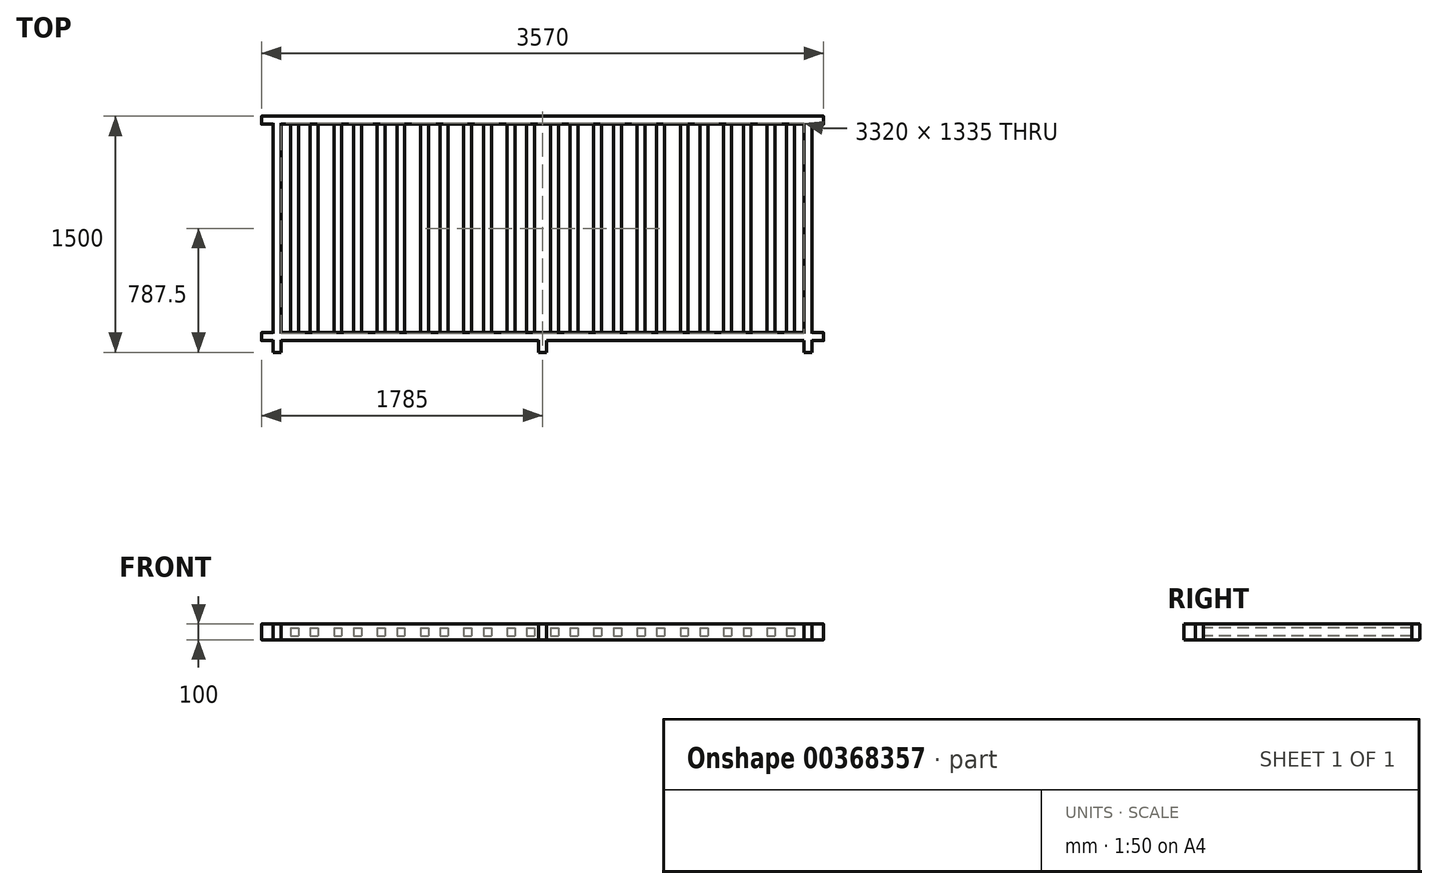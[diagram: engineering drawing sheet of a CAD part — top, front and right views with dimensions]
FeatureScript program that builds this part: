
annotation { "Feature Type Name" : "Feature", "Feature Type Description" : "" }
export const myFeature = defineFeature(function(context is Context, id is Id, definition is map)
    precondition{}
    {
        {
            var Q0;
            Q0=qCreatedBy(makeId("Top.planeOp"),FACE);
            var sketch = newSketch(context, id + "F0", { "sketchPlane" : qUnion([Q0])});
            skLineSegment(sketch, "E0.bottom", {"start": v(0, 0) * mm, "end": v(3570, 0) * mm, "construction": true});
            skLineSegment(sketch, "E0.top", {"start": v(0, 1500) * mm, "end": v(3570, 1500) * mm, "construction": true});
            skLineSegment(sketch, "E0.left", {"start": v(0, 0) * mm, "end": v(0, 1500) * mm, "construction": true});
            skLineSegment(sketch, "E0.right", {"start": v(3570, 0) * mm, "end": v(3570, 1500) * mm, "construction": true});
            skLineSegment(sketch, "E1.bottom", {"start": v(0, 1500) * mm, "end": v(3570, 1500) * mm});
            skLineSegment(sketch, "E1.top", {"start": v(0, 1450) * mm, "end": v(3570, 1450) * mm});
            skLineSegment(sketch, "E1.left", {"start": v(0, 1500) * mm, "end": v(0, 1450) * mm});
            skLineSegment(sketch, "E1.right", {"start": v(3570, 1500) * mm, "end": v(3570, 1450) * mm});
            skLineSegment(sketch, "E2.bottom", {"start": v(0, 125) * mm, "end": v(3570, 125) * mm});
            skLineSegment(sketch, "E2.top", {"start": v(0, 75) * mm, "end": v(3570, 75) * mm});
            skLineSegment(sketch, "E2.left", {"start": v(0, 125) * mm, "end": v(0, 75) * mm});
            skLineSegment(sketch, "E2.right", {"start": v(3570, 125) * mm, "end": v(3570, 75) * mm});
            skLineSegment(sketch, "E3.bottom", {"start": v(75, 1500) * mm, "end": v(125, 1500) * mm});
            skLineSegment(sketch, "E3.top", {"start": v(75, 0) * mm, "end": v(125, 0) * mm});
            skLineSegment(sketch, "E3.left", {"start": v(75, 1500) * mm, "end": v(75, 0) * mm});
            skLineSegment(sketch, "E3.right", {"start": v(125, 1500) * mm, "end": v(125, 0) * mm});
            skLineSegment(sketch, "E4.bottom", {"start": v(3445, 1500) * mm, "end": v(3495, 1500) * mm});
            skLineSegment(sketch, "E4.top", {"start": v(3445, 0) * mm, "end": v(3495, 0) * mm});
            skLineSegment(sketch, "E4.left", {"start": v(3445, 1500) * mm, "end": v(3445, 0) * mm});
            skLineSegment(sketch, "E4.right", {"start": v(3495, 1500) * mm, "end": v(3495, 0) * mm});
            skLineSegment(sketch, "E5.bottom", {"start": v(1810, 0) * mm, "end": v(1760, 0) * mm});
            skLineSegment(sketch, "E5.left", {"start": v(1810, 0) * mm, "end": v(1810, 75) * mm});
            skLineSegment(sketch, "E5.right", {"start": v(1760, 0) * mm, "end": v(1760, 75) * mm});
            skLineSegment(sketch, "E6", {"start": v(3495, 1450) * mm, "end": v(3495, 125) * mm, "construction": true});
            skLineSegment(sketch, "E7", {"start": v(75, 1450) * mm, "end": v(75, 125) * mm, "construction": true});
            skSolve(sketch);
        }
        {
            var Q0;
            Q0=qSketchRegion(id+"F0",true);
            extrude(context, id + "F1", {"entities" : qUnion([Q0]), "depth" : 75 * mm, "hasSecondDirection" : true, "secondDirectionOppositeDirection" : true, "secondDirectionDepth" : 25 * mm});
        }
        {
            var Q0;
            {var subQ0=sQuery(id+"F0.wireOp",EDGE,"E1.top");Q0=makeQuery(id+"F1.opExtrude","CAP_EDGE",EDGE,{"disambiguationData":[OSD([subQ0]),TDD([makeQuery(id+"F0.imprint","IMPRINT",EDGE,{"disambiguationData":[TD([[makeQuery(id+"F0.imprint","INTERSECT",VERTEX,{"derivedFrom":[subQ0,sQuery(id+"F0.wireOp",EDGE,"E3.right")]}),-1.0]])],"derivedFrom":subQ0})])],"isStart":false});}
            var Q1;
            Q1=makeQuery(id+"F1.opExtrude","CAP_EDGE",EDGE,{"disambiguationData":[OSD([sQuery(id+"F0.wireOp",EDGE,"E1.bottom"),sQuery(id+"F0.wireOp",EDGE,"E3.bottom"),sQuery(id+"F0.wireOp",EDGE,"E4.bottom")])],"isStart":false});
            var Q2;
            {var subQ0=sQuery(id+"F0.wireOp",EDGE,"E2.bottom");Q2=makeQuery(id+"F1.opExtrude","CAP_EDGE",EDGE,{"disambiguationData":[OSD([subQ0]),TDD([makeQuery(id+"F0.imprint","IMPRINT",EDGE,{"disambiguationData":[TD([[makeQuery(id+"F0.imprint","INTERSECT",VERTEX,{"derivedFrom":[subQ0,sQuery(id+"F0.wireOp",EDGE,"E3.right")]}),-1.0]])],"derivedFrom":subQ0})])],"isStart":false});}
            var Q3;
            {var subQ0=sQuery(id+"F0.wireOp",EDGE,"E2.top");Q3=makeQuery(id+"F1.opExtrude","CAP_EDGE",EDGE,{"disambiguationData":[OSD([subQ0]),TDD([makeQuery(id+"F0.imprint","IMPRINT",EDGE,{"disambiguationData":[TD([[makeQuery(id+"F0.imprint","INTERSECT",VERTEX,{"derivedFrom":[subQ0,sQuery(id+"F0.wireOp",EDGE,"E3.right")]}),-1.0]])],"derivedFrom":subQ0})])],"isStart":false});}
            var Q4;
            {var subQ0=sQuery(id+"F0.wireOp",EDGE,"E2.top");Q4=makeQuery(id+"F1.opExtrude","CAP_EDGE",EDGE,{"disambiguationData":[OSD([subQ0]),TDD([makeQuery(id+"F0.imprint","IMPRINT",EDGE,{"disambiguationData":[TD([[makeQuery(id+"F0.imprint","INTERSECT",VERTEX,{"derivedFrom":[subQ0,sQuery(id+"F0.wireOp",EDGE,"E2.left")]}),-1.0]])],"derivedFrom":subQ0})])],"isStart":false});}
            var Q5;
            {var subQ0=sQuery(id+"F0.wireOp",EDGE,"E2.bottom");Q5=makeQuery(id+"F1.opExtrude","CAP_EDGE",EDGE,{"disambiguationData":[OSD([subQ0]),TDD([makeQuery(id+"F0.imprint","IMPRINT",EDGE,{"disambiguationData":[TD([[makeQuery(id+"F0.imprint","INTERSECT",VERTEX,{"derivedFrom":[subQ0,sQuery(id+"F0.wireOp",EDGE,"E2.left")]}),-1.0]])],"derivedFrom":subQ0})])],"isStart":false});}
            var Q6;
            {var subQ0=sQuery(id+"F0.wireOp",EDGE,"E2.bottom");Q6=makeQuery(id+"F1.opExtrude","CAP_EDGE",EDGE,{"disambiguationData":[OSD([subQ0]),TDD([makeQuery(id+"F0.imprint","IMPRINT",EDGE,{"disambiguationData":[TD([[makeQuery(id+"F0.imprint","INTERSECT",VERTEX,{"derivedFrom":[subQ0,sQuery(id+"F0.wireOp",EDGE,"E2.right")]}),1.0]])],"derivedFrom":subQ0})])],"isStart":false});}
            var Q7;
            {var subQ0=sQuery(id+"F0.wireOp",EDGE,"E2.top");Q7=makeQuery(id+"F1.opExtrude","CAP_EDGE",EDGE,{"disambiguationData":[OSD([subQ0]),TDD([makeQuery(id+"F0.imprint","IMPRINT",EDGE,{"disambiguationData":[TD([[makeQuery(id+"F0.imprint","INTERSECT",VERTEX,{"derivedFrom":[subQ0,sQuery(id+"F0.wireOp",EDGE,"E2.right")]}),1.0]])],"derivedFrom":subQ0})])],"isStart":false});}
            var Q8;
            {var subQ0=sQuery(id+"F0.wireOp",EDGE,"E1.top");Q8=makeQuery(id+"F1.opExtrude","CAP_EDGE",EDGE,{"disambiguationData":[OSD([subQ0]),TDD([makeQuery(id+"F0.imprint","IMPRINT",EDGE,{"disambiguationData":[TD([[makeQuery(id+"F0.imprint","INTERSECT",VERTEX,{"derivedFrom":[subQ0,sQuery(id+"F0.wireOp",EDGE,"E1.right")]}),1.0]])],"derivedFrom":subQ0})])],"isStart":false});}
            var Q9;
            {var subQ0=sQuery(id+"F0.wireOp",EDGE,"E1.top");Q9=makeQuery(id+"F1.opExtrude","CAP_EDGE",EDGE,{"disambiguationData":[OSD([subQ0]),TDD([makeQuery(id+"F0.imprint","IMPRINT",EDGE,{"disambiguationData":[TD([[makeQuery(id+"F0.imprint","INTERSECT",VERTEX,{"derivedFrom":[subQ0,sQuery(id+"F0.wireOp",EDGE,"E1.left")]}),-1.0]])],"derivedFrom":subQ0})])],"isStart":false});}
            var Q10;
            Q10=makeQuery(id+"F1.opExtrude","CAP_EDGE",EDGE,{"disambiguationData":[OSD([sQuery(id+"F0.wireOp",EDGE,"E1.bottom"),sQuery(id+"F0.wireOp",EDGE,"E3.bottom"),sQuery(id+"F0.wireOp",EDGE,"E4.bottom")])],"isStart":true});
            var Q11;
            {var subQ0=sQuery(id+"F0.wireOp",EDGE,"E1.top");Q11=makeQuery(id+"F1.opExtrude","CAP_EDGE",EDGE,{"disambiguationData":[OSD([subQ0]),TDD([makeQuery(id+"F0.imprint","IMPRINT",EDGE,{"disambiguationData":[TD([[makeQuery(id+"F0.imprint","INTERSECT",VERTEX,{"derivedFrom":[subQ0,sQuery(id+"F0.wireOp",EDGE,"E3.right")]}),-1.0]])],"derivedFrom":subQ0})])],"isStart":true});}
            var Q12;
            {var subQ0=sQuery(id+"F0.wireOp",EDGE,"E1.top");Q12=makeQuery(id+"F1.opExtrude","CAP_EDGE",EDGE,{"disambiguationData":[OSD([subQ0]),TDD([makeQuery(id+"F0.imprint","IMPRINT",EDGE,{"disambiguationData":[TD([[makeQuery(id+"F0.imprint","INTERSECT",VERTEX,{"derivedFrom":[subQ0,sQuery(id+"F0.wireOp",EDGE,"E1.right")]}),1.0]])],"derivedFrom":subQ0})])],"isStart":true});}
            var Q13;
            {var subQ0=sQuery(id+"F0.wireOp",EDGE,"E2.top");Q13=makeQuery(id+"F1.opExtrude","CAP_EDGE",EDGE,{"disambiguationData":[OSD([subQ0]),TDD([makeQuery(id+"F0.imprint","IMPRINT",EDGE,{"disambiguationData":[TD([[makeQuery(id+"F0.imprint","INTERSECT",VERTEX,{"derivedFrom":[subQ0,sQuery(id+"F0.wireOp",EDGE,"E2.right")]}),1.0]])],"derivedFrom":subQ0})])],"isStart":true});}
            var Q14;
            {var subQ0=sQuery(id+"F0.wireOp",EDGE,"E2.bottom");Q14=makeQuery(id+"F1.opExtrude","CAP_EDGE",EDGE,{"disambiguationData":[OSD([subQ0]),TDD([makeQuery(id+"F0.imprint","IMPRINT",EDGE,{"disambiguationData":[TD([[makeQuery(id+"F0.imprint","INTERSECT",VERTEX,{"derivedFrom":[subQ0,sQuery(id+"F0.wireOp",EDGE,"E2.right")]}),1.0]])],"derivedFrom":subQ0})])],"isStart":true});}
            var Q15;
            {var subQ0=sQuery(id+"F0.wireOp",EDGE,"E2.bottom");Q15=makeQuery(id+"F1.opExtrude","CAP_EDGE",EDGE,{"disambiguationData":[OSD([subQ0]),TDD([makeQuery(id+"F0.imprint","IMPRINT",EDGE,{"disambiguationData":[TD([[makeQuery(id+"F0.imprint","INTERSECT",VERTEX,{"derivedFrom":[subQ0,sQuery(id+"F0.wireOp",EDGE,"E3.right")]}),-1.0]])],"derivedFrom":subQ0})])],"isStart":true});}
            var Q16;
            {var subQ0=sQuery(id+"F0.wireOp",EDGE,"E2.top");Q16=makeQuery(id+"F1.opExtrude","CAP_EDGE",EDGE,{"disambiguationData":[OSD([subQ0]),TDD([makeQuery(id+"F0.imprint","IMPRINT",EDGE,{"disambiguationData":[TD([[makeQuery(id+"F0.imprint","INTERSECT",VERTEX,{"derivedFrom":[subQ0,sQuery(id+"F0.wireOp",EDGE,"E3.right")]}),-1.0]])],"derivedFrom":subQ0})])],"isStart":true});}
            var Q17;
            {var subQ0=sQuery(id+"F0.wireOp",EDGE,"E2.bottom");Q17=makeQuery(id+"F1.opExtrude","CAP_EDGE",EDGE,{"disambiguationData":[OSD([subQ0]),TDD([makeQuery(id+"F0.imprint","IMPRINT",EDGE,{"disambiguationData":[TD([[makeQuery(id+"F0.imprint","INTERSECT",VERTEX,{"derivedFrom":[subQ0,sQuery(id+"F0.wireOp",EDGE,"E2.left")]}),-1.0]])],"derivedFrom":subQ0})])],"isStart":true});}
            var Q18;
            {var subQ0=sQuery(id+"F0.wireOp",EDGE,"E2.top");Q18=makeQuery(id+"F1.opExtrude","CAP_EDGE",EDGE,{"disambiguationData":[OSD([subQ0]),TDD([makeQuery(id+"F0.imprint","IMPRINT",EDGE,{"disambiguationData":[TD([[makeQuery(id+"F0.imprint","INTERSECT",VERTEX,{"derivedFrom":[subQ0,sQuery(id+"F0.wireOp",EDGE,"E2.left")]}),-1.0]])],"derivedFrom":subQ0})])],"isStart":true});}
            var Q19;
            {var subQ0=sQuery(id+"F0.wireOp",EDGE,"E1.top");Q19=makeQuery(id+"F1.opExtrude","CAP_EDGE",EDGE,{"disambiguationData":[OSD([subQ0]),TDD([makeQuery(id+"F0.imprint","IMPRINT",EDGE,{"disambiguationData":[TD([[makeQuery(id+"F0.imprint","INTERSECT",VERTEX,{"derivedFrom":[subQ0,sQuery(id+"F0.wireOp",EDGE,"E1.left")]}),-1.0]])],"derivedFrom":subQ0})])],"isStart":true});}
            fillet(context, id + "F2", {"entities" : qUnion([Q0, Q1, Q2, Q3, Q4, Q5, Q6, Q7, Q8, Q9, Q10, Q11, Q12, Q13, Q14, Q15, Q16, Q17, Q18, Q19]), "radius" : 5 * mm, "tangentPropagation" : true, "allowEdgeOverflow" : false});
        }
        {
            var Q0;
            Q0=qCreatedBy(makeId("Top.planeOp"),FACE);
            var sketch = newSketch(context, id + "F3", { "sketchPlane" : qUnion([Q0])});
            skLineSegment(sketch, "E8.bottom", {"start": v(185, 1450) * mm, "end": v(235, 1450) * mm});
            skLineSegment(sketch, "E8.top", {"start": v(185, 125) * mm, "end": v(235, 125) * mm});
            skLineSegment(sketch, "E8.left", {"start": v(185, 1450) * mm, "end": v(185, 125) * mm});
            skLineSegment(sketch, "E8.right", {"start": v(235, 1450) * mm, "end": v(235, 125) * mm});
            skLineSegment(sketch, "E9.bottom", {"start": v(310, 1450) * mm, "end": v(360, 1450) * mm});
            skLineSegment(sketch, "E9.top", {"start": v(310, 125) * mm, "end": v(360, 125) * mm});
            skLineSegment(sketch, "E9.left", {"start": v(310, 1450) * mm, "end": v(310, 125) * mm});
            skLineSegment(sketch, "E9.right", {"start": v(360, 1450) * mm, "end": v(360, 125) * mm});
            skLineSegment(sketch, "E10", {"start": v(235, 125) * mm, "end": v(387, 125) * mm, "construction": true});
            skLineSegment(sketch, "E11", {"start": v(235, 1450) * mm, "end": v(386.34, 1450) * mm, "construction": true});
            skLineSegment(sketch, "E12.1.0.0", {"start": v(635, 1450) * mm, "end": v(635, 125) * mm});
            skLineSegment(sketch, "E12.1.0.1", {"start": v(585, 1450) * mm, "end": v(585, 125) * mm});
            skLineSegment(sketch, "E12.1.0.2", {"start": v(510, 1450) * mm, "end": v(510, 125) * mm});
            skLineSegment(sketch, "E12.1.0.3", {"start": v(460, 1450) * mm, "end": v(460, 125) * mm});
            skLineSegment(sketch, "E12.1.0.4", {"start": v(460, 125) * mm, "end": v(510, 125) * mm});
            skLineSegment(sketch, "E12.1.0.5", {"start": v(460, 1450) * mm, "end": v(510, 1450) * mm});
            skLineSegment(sketch, "E12.1.0.6", {"start": v(585, 125) * mm, "end": v(635, 125) * mm});
            skLineSegment(sketch, "E12.1.0.7", {"start": v(585, 1450) * mm, "end": v(635, 1450) * mm});
            skLineSegment(sketch, "E12.2.0.0", {"start": v(910, 1450) * mm, "end": v(910, 125) * mm});
            skLineSegment(sketch, "E12.2.0.1", {"start": v(860, 1450) * mm, "end": v(860, 125) * mm});
            skLineSegment(sketch, "E12.2.0.2", {"start": v(785, 1450) * mm, "end": v(785, 125) * mm});
            skLineSegment(sketch, "E12.2.0.3", {"start": v(735, 1450) * mm, "end": v(735, 125) * mm});
            skLineSegment(sketch, "E12.2.0.4", {"start": v(735, 125) * mm, "end": v(785, 125) * mm});
            skLineSegment(sketch, "E12.2.0.5", {"start": v(735, 1450) * mm, "end": v(785, 1450) * mm});
            skLineSegment(sketch, "E12.2.0.6", {"start": v(860, 125) * mm, "end": v(910, 125) * mm});
            skLineSegment(sketch, "E12.2.0.7", {"start": v(860, 1450) * mm, "end": v(910, 1450) * mm});
            skLineSegment(sketch, "E12.3.0.0", {"start": v(1185, 1450) * mm, "end": v(1185, 125) * mm});
            skLineSegment(sketch, "E12.3.0.1", {"start": v(1135, 1450) * mm, "end": v(1135, 125) * mm});
            skLineSegment(sketch, "E12.3.0.2", {"start": v(1060, 1450) * mm, "end": v(1060, 125) * mm});
            skLineSegment(sketch, "E12.3.0.3", {"start": v(1010, 1450) * mm, "end": v(1010, 125) * mm});
            skLineSegment(sketch, "E12.3.0.4", {"start": v(1010, 125) * mm, "end": v(1060, 125) * mm});
            skLineSegment(sketch, "E12.3.0.5", {"start": v(1010, 1450) * mm, "end": v(1060, 1450) * mm});
            skLineSegment(sketch, "E12.3.0.6", {"start": v(1135, 125) * mm, "end": v(1185, 125) * mm});
            skLineSegment(sketch, "E12.3.0.7", {"start": v(1135, 1450) * mm, "end": v(1185, 1450) * mm});
            skLineSegment(sketch, "E12.4.0.0", {"start": v(1460, 1450) * mm, "end": v(1460, 125) * mm});
            skLineSegment(sketch, "E12.4.0.1", {"start": v(1410, 1450) * mm, "end": v(1410, 125) * mm});
            skLineSegment(sketch, "E12.4.0.2", {"start": v(1335, 1450) * mm, "end": v(1335, 125) * mm});
            skLineSegment(sketch, "E12.4.0.3", {"start": v(1285, 1450) * mm, "end": v(1285, 125) * mm});
            skLineSegment(sketch, "E12.4.0.4", {"start": v(1285, 125) * mm, "end": v(1335, 125) * mm});
            skLineSegment(sketch, "E12.4.0.5", {"start": v(1285, 1450) * mm, "end": v(1335, 1450) * mm});
            skLineSegment(sketch, "E12.4.0.6", {"start": v(1410, 125) * mm, "end": v(1460, 125) * mm});
            skLineSegment(sketch, "E12.4.0.7", {"start": v(1410, 1450) * mm, "end": v(1460, 1450) * mm});
            skLineSegment(sketch, "E12.5.0.0", {"start": v(1735, 1450) * mm, "end": v(1735, 125) * mm});
            skLineSegment(sketch, "E12.5.0.1", {"start": v(1685, 1450) * mm, "end": v(1685, 125) * mm});
            skLineSegment(sketch, "E12.5.0.2", {"start": v(1610, 1450) * mm, "end": v(1610, 125) * mm});
            skLineSegment(sketch, "E12.5.0.3", {"start": v(1560, 1450) * mm, "end": v(1560, 125) * mm});
            skLineSegment(sketch, "E12.5.0.4", {"start": v(1560, 125) * mm, "end": v(1610, 125) * mm});
            skLineSegment(sketch, "E12.5.0.5", {"start": v(1560, 1450) * mm, "end": v(1610, 1450) * mm});
            skLineSegment(sketch, "E12.5.0.6", {"start": v(1685, 125) * mm, "end": v(1735, 125) * mm});
            skLineSegment(sketch, "E12.5.0.7", {"start": v(1685, 1450) * mm, "end": v(1735, 1450) * mm});
            skLineSegment(sketch, "E12.6.0.0", {"start": v(2010, 1450) * mm, "end": v(2010, 125) * mm});
            skLineSegment(sketch, "E12.6.0.1", {"start": v(1960, 1450) * mm, "end": v(1960, 125) * mm});
            skLineSegment(sketch, "E12.6.0.2", {"start": v(1885, 1450) * mm, "end": v(1885, 125) * mm});
            skLineSegment(sketch, "E12.6.0.3", {"start": v(1835, 1450) * mm, "end": v(1835, 125) * mm});
            skLineSegment(sketch, "E12.6.0.4", {"start": v(1835, 125) * mm, "end": v(1885, 125) * mm});
            skLineSegment(sketch, "E12.6.0.5", {"start": v(1835, 1450) * mm, "end": v(1885, 1450) * mm});
            skLineSegment(sketch, "E12.6.0.6", {"start": v(1960, 125) * mm, "end": v(2010, 125) * mm});
            skLineSegment(sketch, "E12.6.0.7", {"start": v(1960, 1450) * mm, "end": v(2010, 1450) * mm});
            skLineSegment(sketch, "E12.7.0.0", {"start": v(2285, 1450) * mm, "end": v(2285, 125) * mm});
            skLineSegment(sketch, "E12.7.0.1", {"start": v(2235, 1450) * mm, "end": v(2235, 125) * mm});
            skLineSegment(sketch, "E12.7.0.2", {"start": v(2160, 1450) * mm, "end": v(2160, 125) * mm});
            skLineSegment(sketch, "E12.7.0.3", {"start": v(2110, 1450) * mm, "end": v(2110, 125) * mm});
            skLineSegment(sketch, "E12.7.0.4", {"start": v(2110, 125) * mm, "end": v(2160, 125) * mm});
            skLineSegment(sketch, "E12.7.0.5", {"start": v(2110, 1450) * mm, "end": v(2160, 1450) * mm});
            skLineSegment(sketch, "E12.7.0.6", {"start": v(2235, 125) * mm, "end": v(2285, 125) * mm});
            skLineSegment(sketch, "E12.7.0.7", {"start": v(2235, 1450) * mm, "end": v(2285, 1450) * mm});
            skLineSegment(sketch, "E12.8.0.0", {"start": v(2560, 1450) * mm, "end": v(2560, 125) * mm});
            skLineSegment(sketch, "E12.8.0.1", {"start": v(2510, 1450) * mm, "end": v(2510, 125) * mm});
            skLineSegment(sketch, "E12.8.0.2", {"start": v(2435, 1450) * mm, "end": v(2435, 125) * mm});
            skLineSegment(sketch, "E12.8.0.3", {"start": v(2385, 1450) * mm, "end": v(2385, 125) * mm});
            skLineSegment(sketch, "E12.8.0.4", {"start": v(2385, 125) * mm, "end": v(2435, 125) * mm});
            skLineSegment(sketch, "E12.8.0.5", {"start": v(2385, 1450) * mm, "end": v(2435, 1450) * mm});
            skLineSegment(sketch, "E12.8.0.6", {"start": v(2510, 125) * mm, "end": v(2560, 125) * mm});
            skLineSegment(sketch, "E12.8.0.7", {"start": v(2510, 1450) * mm, "end": v(2560, 1450) * mm});
            skLineSegment(sketch, "E12.9.0.0", {"start": v(2835, 1450) * mm, "end": v(2835, 125) * mm});
            skLineSegment(sketch, "E12.9.0.1", {"start": v(2785, 1450) * mm, "end": v(2785, 125) * mm});
            skLineSegment(sketch, "E12.9.0.2", {"start": v(2710, 1450) * mm, "end": v(2710, 125) * mm});
            skLineSegment(sketch, "E12.9.0.3", {"start": v(2660, 1450) * mm, "end": v(2660, 125) * mm});
            skLineSegment(sketch, "E12.9.0.4", {"start": v(2660, 125) * mm, "end": v(2710, 125) * mm});
            skLineSegment(sketch, "E12.9.0.5", {"start": v(2660, 1450) * mm, "end": v(2710, 1450) * mm});
            skLineSegment(sketch, "E12.9.0.6", {"start": v(2785, 125) * mm, "end": v(2835, 125) * mm});
            skLineSegment(sketch, "E12.9.0.7", {"start": v(2785, 1450) * mm, "end": v(2835, 1450) * mm});
            skLineSegment(sketch, "E12.10.0.0", {"start": v(3110, 1450) * mm, "end": v(3110, 125) * mm});
            skLineSegment(sketch, "E12.10.0.1", {"start": v(3060, 1450) * mm, "end": v(3060, 125) * mm});
            skLineSegment(sketch, "E12.10.0.2", {"start": v(2985, 1450) * mm, "end": v(2985, 125) * mm});
            skLineSegment(sketch, "E12.10.0.3", {"start": v(2935, 1450) * mm, "end": v(2935, 125) * mm});
            skLineSegment(sketch, "E12.10.0.4", {"start": v(2935, 125) * mm, "end": v(2985, 125) * mm});
            skLineSegment(sketch, "E12.10.0.5", {"start": v(2935, 1450) * mm, "end": v(2985, 1450) * mm});
            skLineSegment(sketch, "E12.10.0.6", {"start": v(3060, 125) * mm, "end": v(3110, 125) * mm});
            skLineSegment(sketch, "E12.10.0.7", {"start": v(3060, 1450) * mm, "end": v(3110, 1450) * mm});
            skLineSegment(sketch, "E12.11.0.0", {"start": v(3385, 1450) * mm, "end": v(3385, 125) * mm});
            skLineSegment(sketch, "E12.11.0.1", {"start": v(3335, 1450) * mm, "end": v(3335, 125) * mm});
            skLineSegment(sketch, "E12.11.0.2", {"start": v(3260, 1450) * mm, "end": v(3260, 125) * mm});
            skLineSegment(sketch, "E12.11.0.3", {"start": v(3210, 1450) * mm, "end": v(3210, 125) * mm});
            skLineSegment(sketch, "E12.11.0.4", {"start": v(3210, 125) * mm, "end": v(3260, 125) * mm});
            skLineSegment(sketch, "E12.11.0.5", {"start": v(3210, 1450) * mm, "end": v(3260, 1450) * mm});
            skLineSegment(sketch, "E12.11.0.6", {"start": v(3335, 125) * mm, "end": v(3385, 125) * mm});
            skLineSegment(sketch, "E12.11.0.7", {"start": v(3335, 1450) * mm, "end": v(3385, 1450) * mm});
            skLineSegment(sketch, "E12.direction1", {"start": v(185, 125) * mm, "end": v(460, 125) * mm, "construction": true});
            skSolve(sketch);
        }
        {
            var Q0;
            Q0=qSketchRegion(id+"F3",true);
            extrude(context, id + "F4", {"entities" : qUnion([Q0]), "depth" : 50 * mm});
        }
    });
